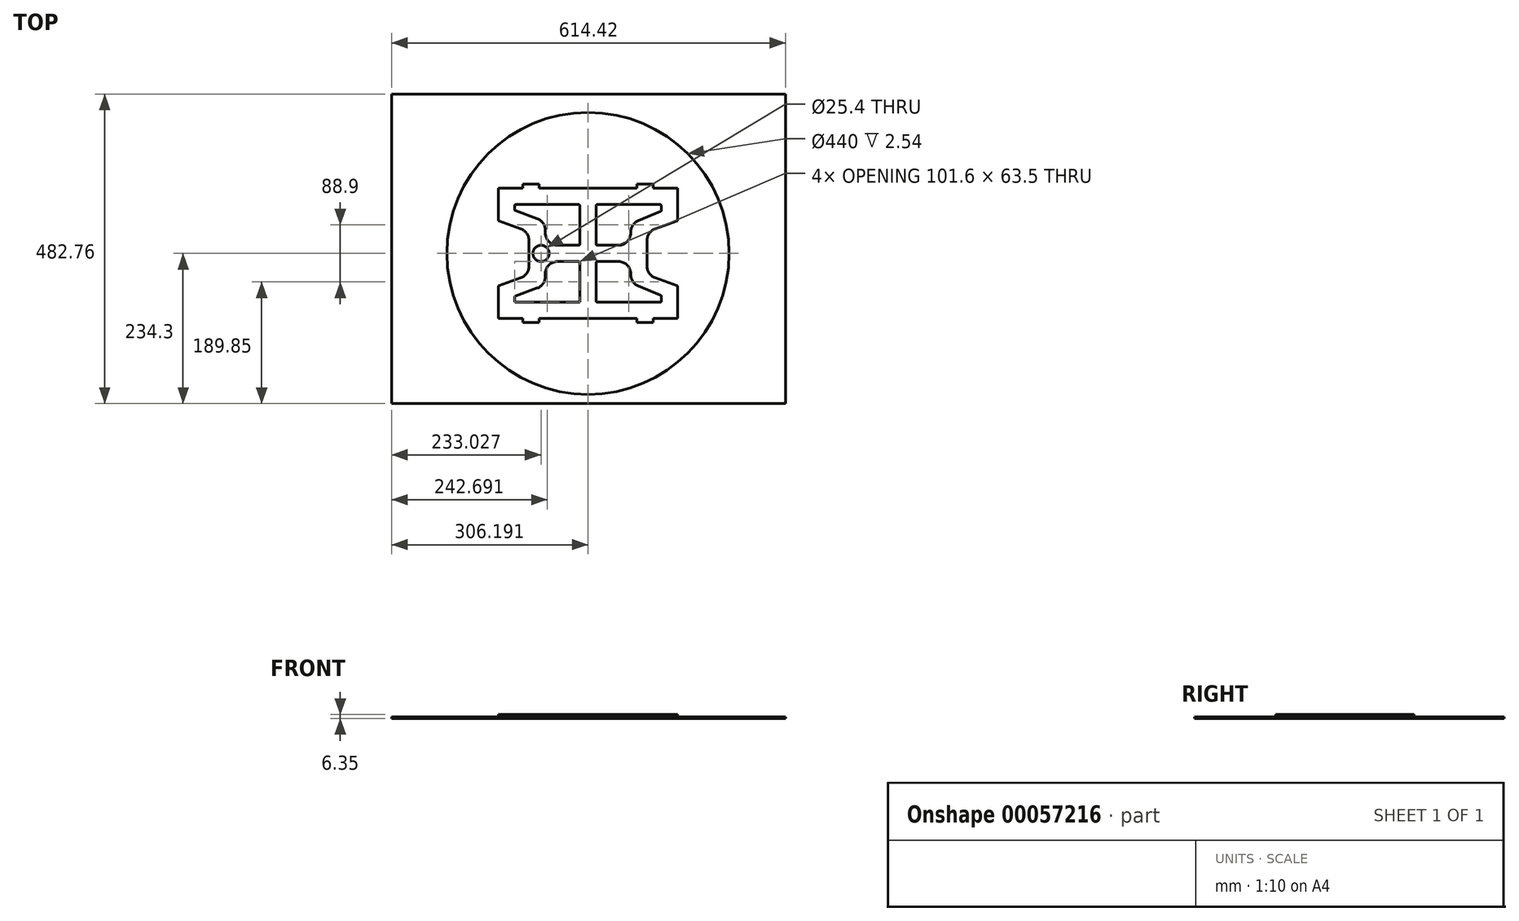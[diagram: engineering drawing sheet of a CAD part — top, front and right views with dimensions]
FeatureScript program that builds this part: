
annotation { "Feature Type Name" : "Feature", "Feature Type Description" : "" }
export const myFeature = defineFeature(function(context is Context, id is Id, definition is map)
    precondition{}
    {
        {
            var Q0;
            Q0=qCreatedBy(makeId("Top.planeOp"),FACE);
            var sketch = newSketch(context, id + "F0", { "sketchPlane" : qUnion([Q0])});
            skCircle(sketch, "E0", {"center": v(3.84, 0) * mm, "radius": 220 * mm});
            skLineSegment(sketch, "E1.bottom", {"start": v(-302.35, 248.46) * mm, "end": v(312.07, 248.46) * mm});
            skLineSegment(sketch, "E1.top", {"start": v(-302.35, -234.3) * mm, "end": v(312.07, -234.3) * mm});
            skLineSegment(sketch, "E1.left", {"start": v(-302.35, 248.46) * mm, "end": v(-302.35, -234.3) * mm});
            skLineSegment(sketch, "E1.right", {"start": v(312.07, 248.46) * mm, "end": v(312.07, -234.3) * mm});
            skSolve(sketch);
        }
        {
            var Q0;
            Q0=makeQuery(id+"F0.imprint","IMPRINT",FACE,{"disambiguationData":[TD([[makeQuery(id+"F0.imprint","IMPRINT",EDGE,{"derivedFrom":sQuery(id+"F0.wireOp",EDGE,"E0")}),1.0]])]});
            var sketch = newSketch(context, id + "F1", { "sketchPlane" : qUnion([Q0])});
            skLineSegment(sketch, "E2.bottom", {"start": v(-135.86, 101.6) * mm, "end": v(143.54, 101.6) * mm});
            skLineSegment(sketch, "E2.top", {"start": v(-135.86, -101.6) * mm, "end": v(143.54, -101.6) * mm});
            skLineSegment(sketch, "E2.left", {"start": v(-135.86, 101.6) * mm, "end": v(-135.86, -101.6) * mm});
            skLineSegment(sketch, "E2.right", {"start": v(143.54, 101.6) * mm, "end": v(143.54, -101.6) * mm});
            skLineSegment(sketch, "E3.bottom", {"start": v(-97.76, -101.6) * mm, "end": v(-72.36, -101.6) * mm});
            skLineSegment(sketch, "E3.top", {"start": v(-97.76, -107.95) * mm, "end": v(-72.36, -107.95) * mm});
            skLineSegment(sketch, "E3.left", {"start": v(-97.76, -101.6) * mm, "end": v(-97.76, -107.95) * mm});
            skLineSegment(sketch, "E3.right", {"start": v(-72.36, -101.6) * mm, "end": v(-72.36, -107.95) * mm});
            skLineSegment(sketch, "E4.bottom", {"start": v(105.44, -101.6) * mm, "end": v(80.04, -101.6) * mm});
            skLineSegment(sketch, "E4.top", {"start": v(105.44, -107.95) * mm, "end": v(80.04, -107.95) * mm});
            skLineSegment(sketch, "E4.left", {"start": v(105.44, -101.6) * mm, "end": v(105.44, -107.95) * mm});
            skLineSegment(sketch, "E4.right", {"start": v(80.04, -101.6) * mm, "end": v(80.04, -107.95) * mm});
            skLineSegment(sketch, "E5.MirrorCS", {"start": v(-97.76, 107.95) * mm, "end": v(-72.36, 107.95) * mm});
            skLineSegment(sketch, "E6.MirrorCS", {"start": v(-97.76, 101.6) * mm, "end": v(-72.36, 101.6) * mm});
            skLineSegment(sketch, "E7.MirrorCS", {"start": v(-97.76, 101.6) * mm, "end": v(-97.76, 107.95) * mm});
            skLineSegment(sketch, "E8.MirrorCS", {"start": v(-72.36, 101.6) * mm, "end": v(-72.36, 107.95) * mm});
            skLineSegment(sketch, "E9.MirrorCS", {"start": v(80.04, 101.6) * mm, "end": v(80.04, 107.95) * mm});
            skLineSegment(sketch, "E10.MirrorCS", {"start": v(105.44, 101.6) * mm, "end": v(105.44, 107.95) * mm});
            skLineSegment(sketch, "E11.MirrorCS", {"start": v(105.44, 107.95) * mm, "end": v(80.04, 107.95) * mm});
            skLineSegment(sketch, "E12.MirrorCS", {"start": v(105.44, 101.6) * mm, "end": v(80.04, 101.6) * mm});
            skLineSegment(sketch, "E13", {"start": v(95.83, 33.4) * mm, "end": v(143.54, 50.85) * mm});
            skLineSegment(sketch, "E14", {"start": v(95.78, -33.63) * mm, "end": v(95.83, 33.4) * mm});
            skLineSegment(sketch, "E15", {"start": v(143.54, -51.02) * mm, "end": v(95.78, -33.63) * mm});
            skLineSegment(sketch, "E16", {"start": v(-88.4, 33.27) * mm, "end": v(-135.86, 51.37) * mm});
            skLineSegment(sketch, "E17", {"start": v(-88.35, -33.49) * mm, "end": v(-88.4, 33.27) * mm});
            skLineSegment(sketch, "E18", {"start": v(-88.35, -33.49) * mm, "end": v(-135.86, -51.13) * mm});
            skCircle(sketch, "E19", {"center": v(-69.32, 0) * mm, "radius": 12.7 * mm});
            skSolve(sketch);
        }
        {
            var Q0;
            Q0=qSketchRegion(id+"F1",true);
            extrude(context, id + "F2", {"entities" : qUnion([Q0]), "depth" : 6.35 * mm});
        }
        {
            var Q0;
            Q0=makeQuery(id+"F0.imprint","IMPRINT",FACE,{"disambiguationData":[TD([[makeQuery(id+"F0.imprint","IMPRINT",EDGE,{"derivedFrom":sQuery(id+"F0.wireOp",EDGE,"E0")}),-1.0]])]});
            extrude(context, id + "F3", {"entities" : qUnion([Q0]), "depth" : 2.54 * mm});
        }
        {
            var Q0;
            Q0=makeQuery(id+"F2.opExtrude","CAP_FACE",FACE,{"disambiguationData":[OSD([sQuery(id+"F1.wireOp",EDGE,"E2.bottom"),sQuery(id+"F1.wireOp",EDGE,"E2.top"),sQuery(id+"F1.wireOp",EDGE,"E2.left"),sQuery(id+"F1.wireOp",EDGE,"E2.right"),sQuery(id+"F1.wireOp",EDGE,"E3.top"),sQuery(id+"F1.wireOp",EDGE,"E3.left"),sQuery(id+"F1.wireOp",EDGE,"E3.right"),sQuery(id+"F1.wireOp",EDGE,"E4.top"),sQuery(id+"F1.wireOp",EDGE,"E4.left"),sQuery(id+"F1.wireOp",EDGE,"E4.right"),sQuery(id+"F1.wireOp",EDGE,"E5.MirrorCS"),sQuery(id+"F1.wireOp",EDGE,"E7.MirrorCS"),sQuery(id+"F1.wireOp",EDGE,"E8.MirrorCS"),sQuery(id+"F1.wireOp",EDGE,"E9.MirrorCS"),sQuery(id+"F1.wireOp",EDGE,"E10.MirrorCS"),sQuery(id+"F1.wireOp",EDGE,"E11.MirrorCS")])],"isStart":false});
            var sketch = newSketch(context, id + "F4", { "sketchPlane" : qUnion([Q0])});
            skLineSegment(sketch, "E20", {"start": v(143.54, 50.8) * mm, "end": v(108.34, 37.99) * mm});
            skLineSegment(sketch, "E21", {"start": v(143.54, -50.8) * mm, "end": v(108.34, -37.99) * mm});
            skLineSegment(sketch, "E22", {"start": v(95.8, -20.09) * mm, "end": v(95.8, 20.09) * mm});
            skLineSegment(sketch, "E23", {"start": v(-135.86, 50.8) * mm, "end": v(-100.66, 37.99) * mm});
            skLineSegment(sketch, "E24", {"start": v(-135.86, -50.8) * mm, "end": v(-100.66, -37.99) * mm});
            skLineSegment(sketch, "E25", {"start": v(-88.12, 20.09) * mm, "end": v(-88.12, -20.09) * mm});
            skPoint(sketch, "E26.visualSharp", {"position": v(-88.12, 33.43) * mm});
            skArc(sketch, "E26.filletArc", {"start": v(-88.12, 20.09) * mm, "mid": v(-91.57, 31.01) * mm, "end": v(-100.66, 37.99) * mm});
            skPoint(sketch, "E27.visualSharp", {"position": v(-88.12, -33.43) * mm});
            skArc(sketch, "E27.filletArc", {"start": v(-100.66, -37.99) * mm, "mid": v(-91.57, -31.01) * mm, "end": v(-88.12, -20.09) * mm});
            skPoint(sketch, "E28.visualSharp", {"position": v(95.8, 33.43) * mm});
            skArc(sketch, "E28.filletArc", {"start": v(108.34, 37.99) * mm, "mid": v(99.25, 31.01) * mm, "end": v(95.8, 20.09) * mm});
            skPoint(sketch, "E29.visualSharp", {"position": v(95.8, -33.43) * mm});
            skArc(sketch, "E29.filletArc", {"start": v(95.8, -20.09) * mm, "mid": v(99.25, -31.01) * mm, "end": v(108.34, -37.99) * mm});
            skSolve(sketch);
        }
        {
            var Q0;
            {var subQ2=sQuery(id+"F4.wireOp",EDGE,"E20");Q0=makeQuery(id+"F4.imprint","IMPRINT",FACE,{"disambiguationData":[TD([[makeQuery(id+"F4.imprint","IMPRINT",EDGE,{"derivedFrom":subQ2}),1.0]])]});}
            var Q1;
            {var subQ2=sQuery(id+"F4.wireOp",EDGE,"E23");Q1=makeQuery(id+"F4.imprint","IMPRINT",FACE,{"disambiguationData":[TD([[makeQuery(id+"F4.imprint","IMPRINT",EDGE,{"derivedFrom":subQ2}),-1.0]])]});}
            extrude(context, id + "F5", {"entities" : qUnion([Q0, Q1]), "operationType" : NewBodyOperationType.REMOVE, "oppositeDirection" : true, "depth" : 25.4 * mm});
        }
        {
            var Q0;
            Q0=makeQuery(id+"F2.opExtrude","CAP_FACE",FACE,{"disambiguationData":[OSD([sQuery(id+"F1.wireOp",EDGE,"E2.bottom"),sQuery(id+"F1.wireOp",EDGE,"E2.top"),sQuery(id+"F1.wireOp",EDGE,"E2.left"),sQuery(id+"F1.wireOp",EDGE,"E2.right"),sQuery(id+"F1.wireOp",EDGE,"E3.top"),sQuery(id+"F1.wireOp",EDGE,"E3.left"),sQuery(id+"F1.wireOp",EDGE,"E3.right"),sQuery(id+"F1.wireOp",EDGE,"E4.top"),sQuery(id+"F1.wireOp",EDGE,"E4.left"),sQuery(id+"F1.wireOp",EDGE,"E4.right"),sQuery(id+"F1.wireOp",EDGE,"E5.MirrorCS"),sQuery(id+"F1.wireOp",EDGE,"E7.MirrorCS"),sQuery(id+"F1.wireOp",EDGE,"E8.MirrorCS"),sQuery(id+"F1.wireOp",EDGE,"E9.MirrorCS"),sQuery(id+"F1.wireOp",EDGE,"E10.MirrorCS"),sQuery(id+"F1.wireOp",EDGE,"E11.MirrorCS")])],"isStart":false});
            var sketch = newSketch(context, id + "F6", { "sketchPlane" : qUnion([Q0])});
            skLineSegment(sketch, "E30", {"start": v(117.01, 65.22) * mm, "end": v(82.18, 50.8) * mm});
            skLineSegment(sketch, "E31", {"start": v(70.41, -33.2) * mm, "end": v(70.41, -31.75) * mm});
            skLineSegment(sketch, "E32", {"start": v(117.01, -65.22) * mm, "end": v(82.18, -50.8) * mm});
            skLineSegment(sketch, "E33", {"start": v(-62.72, 31.75) * mm, "end": v(-62.72, 36.24) * mm});
            skLineSegment(sketch, "E34", {"start": v(-109.26, 66.52) * mm, "end": v(-75.26, 54.14) * mm});
            skLineSegment(sketch, "E35", {"start": v(-109.26, -66.52) * mm, "end": v(-75.26, -54.14) * mm});
            skLineSegment(sketch, "E36", {"start": v(3.84, -101.6) * mm, "end": v(3.84, 101.6) * mm, "construction": true});
            skLineSegment(sketch, "E37", {"start": v(-62.72, 0) * mm, "end": v(70.41, 0) * mm, "construction": true});
            skLineSegment(sketch, "E38", {"start": v(-43.67, -12.7) * mm, "end": v(-10.69, -12.7) * mm});
            skLineSegment(sketch, "E39.MirrorCS", {"start": v(-43.67, 12.7) * mm, "end": v(-10.69, 12.7) * mm});
            skLineSegment(sketch, "E40", {"start": v(16.54, 74.37) * mm, "end": v(16.54, 14.53) * mm});
            skLineSegment(sketch, "E41.MirrorCS", {"start": v(-8.86, 74.37) * mm, "end": v(-8.86, 14.53) * mm});
            skLineSegment(sketch, "E42", {"start": v(-110.46, -68.24) * mm, "end": v(-110.46, -74.37) * mm});
            skLineSegment(sketch, "E43", {"start": v(18.37, -76.2) * mm, "end": v(116.31, -76.2) * mm});
            skLineSegment(sketch, "E44", {"start": v(118.14, -74.37) * mm, "end": v(118.14, -66.9) * mm});
            skLineSegment(sketch, "E45.MirrorCS", {"start": v(-110.46, 68.24) * mm, "end": v(-110.46, 74.37) * mm});
            skLineSegment(sketch, "E46.MirrorCS", {"start": v(-108.63, 76.2) * mm, "end": v(-10.69, 76.2) * mm});
            skLineSegment(sketch, "E47.MirrorCS", {"start": v(118.14, 74.37) * mm, "end": v(118.14, 66.9) * mm});
            skPoint(sketch, "E48.visualSharp", {"position": v(70.41, 45.93) * mm});
            skArc(sketch, "E48.filletArc", {"start": v(82.18, 50.8) * mm, "mid": v(73.63, 43.79) * mm, "end": v(70.41, 33.2) * mm});
            skPoint(sketch, "E49.visualSharp", {"position": v(70.41, -45.93) * mm});
            skArc(sketch, "E49.filletArc", {"start": v(70.41, -33.2) * mm, "mid": v(73.63, -43.79) * mm, "end": v(82.18, -50.8) * mm});
            skPoint(sketch, "E50.newPointA", {"position": v(143.54, -76.2) * mm});
            skPoint(sketch, "E50.newPointB", {"position": v(118.14, -66.96) * mm});
            skArc(sketch, "E50.filletArc", {"start": v(118.14, -66.9) * mm, "mid": v(117.83, -65.9) * mm, "end": v(117.01, -65.22) * mm});
            skPoint(sketch, "E51.newPointA", {"position": v(118.14, 66.96) * mm});
            skPoint(sketch, "E51.newPointB", {"position": v(143.54, 76.2) * mm});
            skArc(sketch, "E51.filletArc", {"start": v(117.01, 65.22) * mm, "mid": v(117.83, 65.9) * mm, "end": v(118.14, 66.9) * mm});
            skArc(sketch, "E52.filletArc", {"start": v(118.14, 74.37) * mm, "mid": v(117.6, 75.66) * mm, "end": v(116.31, 76.2) * mm});
            skPoint(sketch, "E53.visualSharp", {"position": v(-62.72, 49.58) * mm});
            skArc(sketch, "E53.filletArc", {"start": v(-62.72, 36.24) * mm, "mid": v(-66.17, 47.17) * mm, "end": v(-75.26, 54.14) * mm});
            skPoint(sketch, "E54.visualSharp", {"position": v(-62.72, -49.58) * mm});
            skArc(sketch, "E54.filletArc", {"start": v(-75.26, -54.14) * mm, "mid": v(-66.17, -47.17) * mm, "end": v(-62.72, -36.24) * mm});
            skPoint(sketch, "E55.newPointA", {"position": v(-135.86, 76.2) * mm});
            skPoint(sketch, "E55.newPointB", {"position": v(-110.46, 66.96) * mm});
            skArc(sketch, "E55.filletArc", {"start": v(-110.46, 68.24) * mm, "mid": v(-110.13, 67.19) * mm, "end": v(-109.26, 66.52) * mm});
            skPoint(sketch, "E56.visualSharp", {"position": v(-110.46, 76.2) * mm});
            skArc(sketch, "E56.filletArc", {"start": v(-108.63, 76.2) * mm, "mid": v(-109.92, 75.66) * mm, "end": v(-110.46, 74.37) * mm});
            skPoint(sketch, "E57.newPointB", {"position": v(-8.86, 101.6) * mm});
            skArc(sketch, "E57.filletArc", {"start": v(-8.86, 74.37) * mm, "mid": v(-9.4, 75.66) * mm, "end": v(-10.69, 76.2) * mm});
            skPoint(sketch, "E58.newPointA", {"position": v(-8.86, -101.6) * mm});
            skPoint(sketch, "E58.newPointB", {"position": v(70.41, 12.7) * mm});
            skArc(sketch, "E58.filletArc", {"start": v(-10.69, 12.7) * mm, "mid": v(-9.4, 13.24) * mm, "end": v(-8.86, 14.53) * mm});
            skPoint(sketch, "E59.newPointB", {"position": v(-62.72, 12.7) * mm});
            skArc(sketch, "E59.filletArc", {"start": v(-62.72, 31.75) * mm, "mid": v(-57.14, 18.28) * mm, "end": v(-43.67, 12.7) * mm});
            skLineSegment(sketch, "E60", {"start": v(-62.72, -36.24) * mm, "end": v(-62.72, -31.75) * mm});
            skLineSegment(sketch, "E61", {"start": v(-8.86, -14.53) * mm, "end": v(-8.86, -76.2) * mm});
            skPoint(sketch, "E61.endSnap0", {"position": v(3.84, -76.2) * mm});
            skPoint(sketch, "E62.newPointA", {"position": v(70.41, -12.7) * mm});
            skPoint(sketch, "E62.newPointB", {"position": v(-8.86, -12.7) * mm});
            skArc(sketch, "E62.filletArc", {"start": v(-8.86, -14.53) * mm, "mid": v(-9.4, -13.24) * mm, "end": v(-10.69, -12.7) * mm});
            skPoint(sketch, "E63.visualSharp", {"position": v(-62.72, -12.7) * mm});
            skArc(sketch, "E63.filletArc", {"start": v(-43.67, -12.7) * mm, "mid": v(-57.14, -18.28) * mm, "end": v(-62.72, -31.75) * mm});
            skLineSegment(sketch, "E64", {"start": v(18.37, -12.7) * mm, "end": v(51.36, -12.7) * mm});
            skLineSegment(sketch, "E65", {"start": v(51.36, 12.7) * mm, "end": v(18.37, 12.7) * mm});
            skPoint(sketch, "E66.newPointA", {"position": v(16.54, -101.6) * mm});
            skArc(sketch, "E66.filletArc", {"start": v(16.54, 14.53) * mm, "mid": v(17.08, 13.24) * mm, "end": v(18.37, 12.7) * mm});
            skLineSegment(sketch, "E67", {"start": v(16.54, -14.53) * mm, "end": v(16.54, -74.37) * mm});
            skPoint(sketch, "E68.visualSharp", {"position": v(16.54, -12.7) * mm});
            skArc(sketch, "E68.filletArc", {"start": v(18.37, -12.7) * mm, "mid": v(17.08, -13.24) * mm, "end": v(16.54, -14.53) * mm});
            skPoint(sketch, "E69.newPointB", {"position": v(-110.46, -76.2) * mm});
            skArc(sketch, "E69.filletArc", {"start": v(16.54, -74.37) * mm, "mid": v(17.08, -75.66) * mm, "end": v(18.37, -76.2) * mm});
            skPoint(sketch, "E70.visualSharp", {"position": v(118.14, -76.2) * mm});
            skArc(sketch, "E70.filletArc", {"start": v(116.31, -76.2) * mm, "mid": v(117.6, -75.66) * mm, "end": v(118.14, -74.37) * mm});
            skLineSegment(sketch, "E71", {"start": v(-8.86, -76.2) * mm, "end": v(-108.63, -76.2) * mm});
            skArc(sketch, "E72.filletArc", {"start": v(-110.46, -74.37) * mm, "mid": v(-109.92, -75.66) * mm, "end": v(-108.63, -76.2) * mm});
            skPoint(sketch, "E73.newPointA", {"position": v(-110.46, -66.96) * mm});
            skPoint(sketch, "E73.newPointB", {"position": v(-135.86, -76.2) * mm});
            skArc(sketch, "E73.filletArc", {"start": v(-109.26, -66.52) * mm, "mid": v(-110.13, -67.19) * mm, "end": v(-110.46, -68.24) * mm});
            skLineSegment(sketch, "E74", {"start": v(116.31, 76.2) * mm, "end": v(18.37, 76.2) * mm});
            skPoint(sketch, "E75.newPointB", {"position": v(16.54, 101.6) * mm});
            skArc(sketch, "E75.filletArc", {"start": v(18.37, 76.2) * mm, "mid": v(17.08, 75.66) * mm, "end": v(16.54, 74.37) * mm});
            skArc(sketch, "E76.filletArc", {"start": v(70.41, -31.75) * mm, "mid": v(64.83, -18.28) * mm, "end": v(51.36, -12.7) * mm});
            skLineSegment(sketch, "E77", {"start": v(70.41, 31.75) * mm, "end": v(70.41, 33.2) * mm});
            skArc(sketch, "E78.filletArc", {"start": v(51.36, 12.7) * mm, "mid": v(64.83, 18.28) * mm, "end": v(70.41, 31.75) * mm});
            skSolve(sketch);
        }
        {
            var Q0;
            {var subQ0=sQuery(id+"F6.wireOp",EDGE,"E42");Q0=makeQuery(id+"F6.imprint","IMPRINT",FACE,{"disambiguationData":[TD([[makeQuery(id+"F6.imprint","IMPRINT",EDGE,{"derivedFrom":subQ0}),1.0]])]});}
            var Q1;
            {var subQ3=sQuery(id+"F6.wireOp",EDGE,"E45.MirrorCS");Q1=makeQuery(id+"F6.imprint","IMPRINT",FACE,{"disambiguationData":[TD([[makeQuery(id+"F6.imprint","IMPRINT",EDGE,{"derivedFrom":subQ3}),-1.0]])]});}
            var Q2;
            {var subQ0=sQuery(id+"F6.wireOp",EDGE,"E47.MirrorCS");Q2=makeQuery(id+"F6.imprint","IMPRINT",FACE,{"disambiguationData":[TD([[makeQuery(id+"F6.imprint","IMPRINT",EDGE,{"derivedFrom":subQ0}),-1.0]])]});}
            var Q3;
            {var subQ5=sQuery(id+"F6.wireOp",EDGE,"E44");Q3=makeQuery(id+"F6.imprint","IMPRINT",FACE,{"disambiguationData":[TD([[makeQuery(id+"F6.imprint","IMPRINT",EDGE,{"derivedFrom":subQ5}),1.0]])]});}
            extrude(context, id + "F7", {"entities" : qUnion([Q0, Q1, Q2, Q3]), "operationType" : NewBodyOperationType.REMOVE, "oppositeDirection" : true, "depth" : 25.4 * mm});
        }
    });
